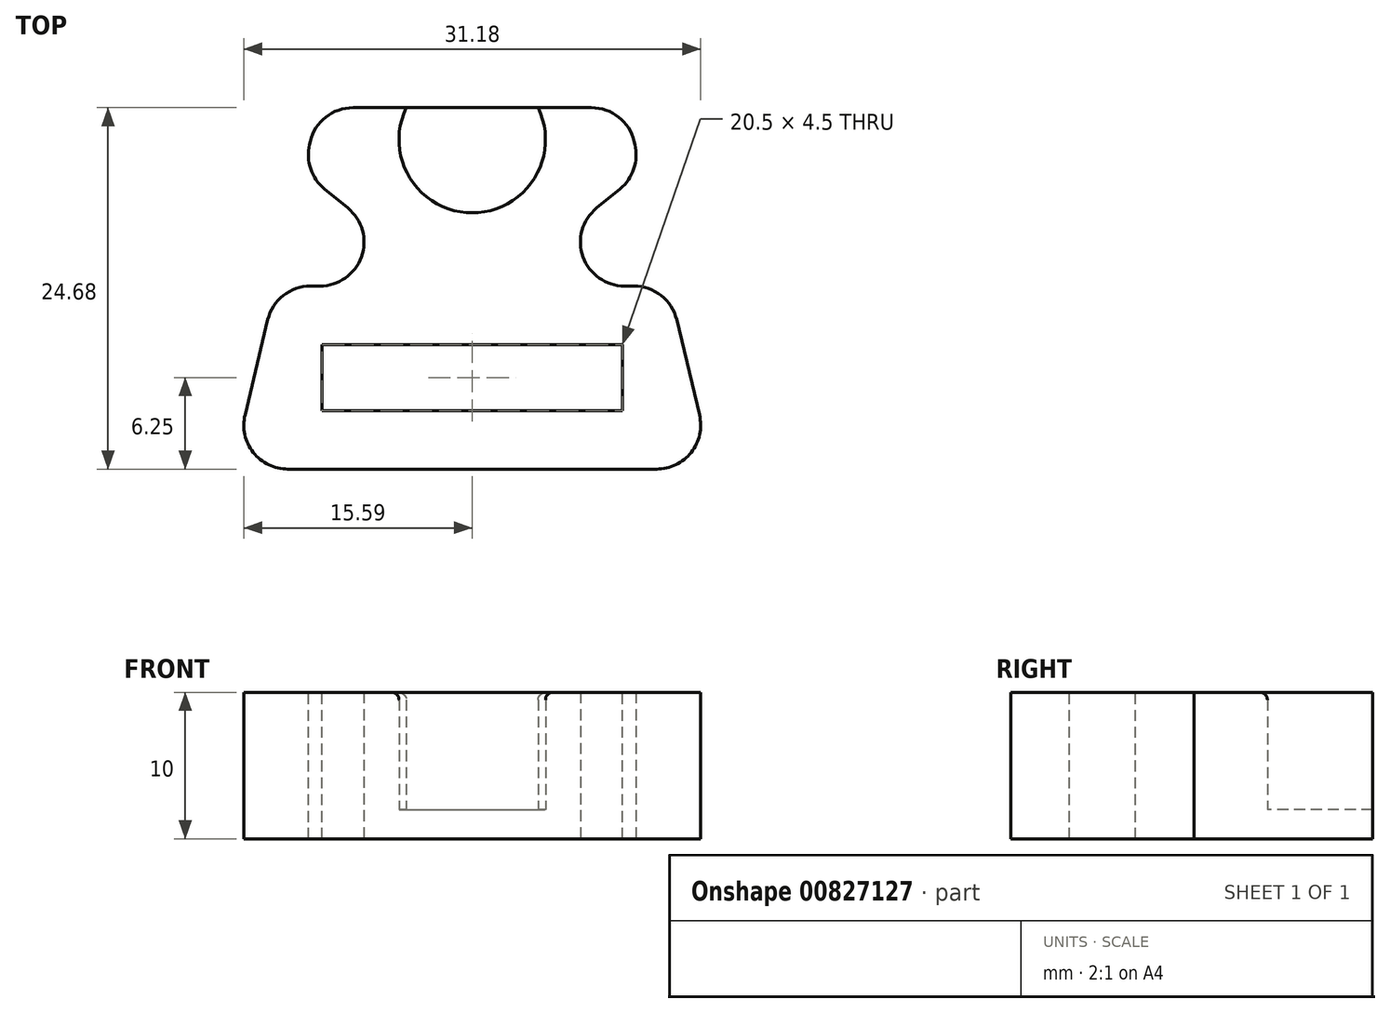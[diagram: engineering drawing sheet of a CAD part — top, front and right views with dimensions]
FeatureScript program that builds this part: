
annotation { "Feature Type Name" : "Feature", "Feature Type Description" : "" }
export const myFeature = defineFeature(function(context is Context, id is Id, definition is map)
    precondition{}
    {
        {
            var Q0;
            Q0=qCreatedBy(makeId("Top.planeOp"),FACE);
            var sketch = newSketch(context, id + "F0", { "sketchPlane" : qUnion([Q0])});
            skArc(sketch, "E0", {"start": v(-4.5, 2.18) * mm, "mid": v(0, -5) * mm, "end": v(4.5, 2.18) * mm});
            skLineSegment(sketch, "E1", {"start": v(4.5, 2.18) * mm, "end": v(10.5, 2.18) * mm});
            skLineSegment(sketch, "E2", {"start": v(-4.5, 2.18) * mm, "end": v(-10.5, 2.18) * mm});
            skLineSegment(sketch, "E3", {"start": v(-10.5, 2.18) * mm, "end": v(-16.4, -22.5) * mm});
            skLineSegment(sketch, "E4", {"start": v(-16.4, -22.5) * mm, "end": v(16.4, -22.5) * mm});
            skLineSegment(sketch, "E5", {"start": v(16.4, -22.5) * mm, "end": v(10.5, 2.18) * mm});
            skLineSegment(sketch, "E6.bottom", {"start": v(10.25, -18.5) * mm, "end": v(-10.25, -18.5) * mm});
            skLineSegment(sketch, "E6.top", {"start": v(10.25, -14) * mm, "end": v(-10.25, -14) * mm});
            skLineSegment(sketch, "E6.left", {"start": v(10.25, -18.5) * mm, "end": v(10.25, -14) * mm});
            skLineSegment(sketch, "E6.right", {"start": v(-10.25, -18.5) * mm, "end": v(-10.25, -14) * mm});
            skPoint(sketch, "E6.middle", {"position": v(0, -16.25) * mm});
            skLineSegment(sketch, "E7", {"start": v(0, 0) * mm, "end": v(5, 0) * mm, "construction": true});
            skLineSegment(sketch, "E8", {"start": v(-4.5, 2.18) * mm, "end": v(4.5, 2.18) * mm});
            skLineSegment(sketch, "E9", {"start": v(11.54, -2.17) * mm, "end": v(2, -10) * mm});
            skLineSegment(sketch, "E10", {"start": v(2, -10) * mm, "end": v(13.4, -10) * mm});
            skLineSegment(sketch, "E11", {"start": v(-11.54, -2.17) * mm, "end": v(-2, -10) * mm});
            skLineSegment(sketch, "E12", {"start": v(-2, -10) * mm, "end": v(-13.4, -10) * mm});
            skLineSegment(sketch, "E13", {"start": v(0, -16.25) * mm, "end": v(2, -10) * mm, "construction": true});
            skLineSegment(sketch, "E14", {"start": v(-2, -10) * mm, "end": v(0, -16.25) * mm, "construction": true});
            skSolve(sketch);
        }
        {
            var Q0;
            Q0=makeQuery(id+"F0.imprint","IMPRINT",FACE,{"disambiguationData":[TD([[makeQuery(id+"F0.imprint","IMPRINT",EDGE,{"derivedFrom":sQuery(id+"F0.wireOp",EDGE,"E0")}),-1.0]])]});
            var Q1;
            Q1=makeQuery(id+"F0.imprint","IMPRINT",FACE,{"disambiguationData":[TD([[makeQuery(id+"F0.imprint","IMPRINT",EDGE,{"derivedFrom":sQuery(id+"F0.wireOp",EDGE,"E0")}),1.0]])]});
            extrude(context, id + "F1", {"entities" : qUnion([Q0, Q1]), "oppositeDirection" : true, "depth" : 5 * mm, "offsetDistance" : 25 * mm});
        }
        {
            var Q0;
            Q0=makeQuery(id+"F0.imprint","IMPRINT",FACE,{"disambiguationData":[TD([[makeQuery(id+"F0.imprint","IMPRINT",EDGE,{"derivedFrom":sQuery(id+"F0.wireOp",EDGE,"E0")}),-1.0]])]});
            extrude(context, id + "F2", {"entities" : qUnion([Q0]), "operationType" : NewBodyOperationType.ADD, "depth" : 5 * mm, "offsetDistance" : 25 * mm});
        }
        {
            var Q0;
            {var subQ0=sQuery(id+"F0.wireOp",EDGE,"E4");var subQ1=sQuery(id+"F0.wireOp",EDGE,"E3");Q0=makeQuery(id+"F2.boolean.opBoolean","MERGE",EDGE,{"derivedFrom":[makeQuery(id+"F1.opExtrude","SWEPT_EDGE",EDGE,{"disambiguationData":[OSD([subQ1,subQ0])]}),makeQuery(id+"F2.opExtrude","SWEPT_EDGE",EDGE,{"disambiguationData":[OSD([subQ1,subQ0])]})]});}
            var Q1;
            {var subQ0=sQuery(id+"F0.wireOp",EDGE,"E5");var subQ1=sQuery(id+"F0.wireOp",EDGE,"E4");Q1=makeQuery(id+"F2.boolean.opBoolean","MERGE",EDGE,{"derivedFrom":[makeQuery(id+"F1.opExtrude","SWEPT_EDGE",EDGE,{"disambiguationData":[OSD([subQ1,subQ0])]}),makeQuery(id+"F2.opExtrude","SWEPT_EDGE",EDGE,{"disambiguationData":[OSD([subQ1,subQ0])]})]});}
            var Q2;
            {var subQ0=sQuery(id+"F0.wireOp",EDGE,"E3");var subQ1=sQuery(id+"F0.wireOp",EDGE,"E2");Q2=makeQuery(id+"F2.boolean.opBoolean","MERGE",EDGE,{"derivedFrom":[makeQuery(id+"F1.opExtrude","SWEPT_EDGE",EDGE,{"disambiguationData":[OSD([subQ1,subQ0])]}),makeQuery(id+"F2.opExtrude","SWEPT_EDGE",EDGE,{"disambiguationData":[OSD([subQ1,subQ0])]})]});}
            var Q3;
            {var subQ0=sQuery(id+"F0.wireOp",EDGE,"E5");var subQ1=sQuery(id+"F0.wireOp",EDGE,"E1");Q3=makeQuery(id+"F2.boolean.opBoolean","MERGE",EDGE,{"derivedFrom":[makeQuery(id+"F1.opExtrude","SWEPT_EDGE",EDGE,{"disambiguationData":[OSD([subQ1,subQ0])]}),makeQuery(id+"F2.opExtrude","SWEPT_EDGE",EDGE,{"disambiguationData":[OSD([subQ1,subQ0])]})]});}
            var Q4;
            {var subQ0=sQuery(id+"F0.wireOp",EDGE,"E12");var subQ1=sQuery(id+"F0.wireOp",EDGE,"E11");Q4=makeQuery(id+"F2.boolean.opBoolean","MERGE",EDGE,{"derivedFrom":[makeQuery(id+"F1.opExtrude","SWEPT_EDGE",EDGE,{"disambiguationData":[OSD([subQ1,subQ0])]}),makeQuery(id+"F2.opExtrude","SWEPT_EDGE",EDGE,{"disambiguationData":[OSD([subQ1,subQ0])]})]});}
            var Q5;
            {var subQ0=sQuery(id+"F0.wireOp",EDGE,"E12");var subQ1=sQuery(id+"F0.wireOp",EDGE,"E3");Q5=makeQuery(id+"F2.boolean.opBoolean","MERGE",EDGE,{"derivedFrom":[makeQuery(id+"F1.opExtrude","SWEPT_EDGE",EDGE,{"disambiguationData":[OSD([subQ1,subQ0])]}),makeQuery(id+"F2.opExtrude","SWEPT_EDGE",EDGE,{"disambiguationData":[OSD([subQ1,subQ0])]})]});}
            var Q6;
            {var subQ0=sQuery(id+"F0.wireOp",EDGE,"E11");var subQ1=sQuery(id+"F0.wireOp",EDGE,"E3");Q6=makeQuery(id+"F2.boolean.opBoolean","MERGE",EDGE,{"derivedFrom":[makeQuery(id+"F1.opExtrude","SWEPT_EDGE",EDGE,{"disambiguationData":[OSD([subQ1,subQ0])]}),makeQuery(id+"F2.opExtrude","SWEPT_EDGE",EDGE,{"disambiguationData":[OSD([subQ1,subQ0])]})]});}
            var Q7;
            {var subQ0=sQuery(id+"F0.wireOp",EDGE,"E9");var subQ1=sQuery(id+"F0.wireOp",EDGE,"E5");Q7=makeQuery(id+"F2.boolean.opBoolean","MERGE",EDGE,{"derivedFrom":[makeQuery(id+"F1.opExtrude","SWEPT_EDGE",EDGE,{"disambiguationData":[OSD([subQ1,subQ0])]}),makeQuery(id+"F2.opExtrude","SWEPT_EDGE",EDGE,{"disambiguationData":[OSD([subQ1,subQ0])]})]});}
            var Q8;
            {var subQ0=sQuery(id+"F0.wireOp",EDGE,"E10");var subQ1=sQuery(id+"F0.wireOp",EDGE,"E5");Q8=makeQuery(id+"F2.boolean.opBoolean","MERGE",EDGE,{"derivedFrom":[makeQuery(id+"F1.opExtrude","SWEPT_EDGE",EDGE,{"disambiguationData":[OSD([subQ1,subQ0])]}),makeQuery(id+"F2.opExtrude","SWEPT_EDGE",EDGE,{"disambiguationData":[OSD([subQ1,subQ0])]})]});}
            var Q9;
            {var subQ0=sQuery(id+"F0.wireOp",EDGE,"E10");var subQ1=sQuery(id+"F0.wireOp",EDGE,"E9");Q9=makeQuery(id+"F2.boolean.opBoolean","MERGE",EDGE,{"derivedFrom":[makeQuery(id+"F1.opExtrude","SWEPT_EDGE",EDGE,{"disambiguationData":[OSD([subQ1,subQ0])]}),makeQuery(id+"F2.opExtrude","SWEPT_EDGE",EDGE,{"disambiguationData":[OSD([subQ1,subQ0])]})]});}
            fillet(context, id + "F3", {"entities" : qUnion([Q0, Q1, Q2, Q3, Q4, Q5, Q6, Q7, Q8, Q9]), "tangentPropagation" : true, "radius" : 3 * mm, "defaultsChanged" : true, "vertexSettings" : [], "allowEdgeOverflow" : false});
        }
        {
            var Q0;
            Q0=makeQuery(id+"F2.opExtrude","CAP_EDGE",EDGE,{"disambiguationData":[OSD([sQuery(id+"F0.wireOp",EDGE,"E0")])],"isStart":false});
            fillet(context, id + "F4", {"entities" : qUnion([Q0]), "tangentPropagation" : true, "radius" : 0.5 * mm, "defaultsChanged" : true, "vertexSettings" : [], "allowEdgeOverflow" : false});
        }
        {
            var Q0;
            Q0=makeQuery(id+"F1.opExtrude","CAP_FACE",FACE,{"disambiguationData":[OSD([sQuery(id+"F0.wireOp",EDGE,"E1"),sQuery(id+"F0.wireOp",EDGE,"E2"),sQuery(id+"F0.wireOp",EDGE,"E3"),sQuery(id+"F0.wireOp",EDGE,"E4"),sQuery(id+"F0.wireOp",EDGE,"E5"),sQuery(id+"F0.wireOp",EDGE,"E6.bottom"),sQuery(id+"F0.wireOp",EDGE,"E6.top"),sQuery(id+"F0.wireOp",EDGE,"E6.left"),sQuery(id+"F0.wireOp",EDGE,"E6.right"),sQuery(id+"F0.wireOp",EDGE,"E8")])],"isStart":true});
            extrude(context, id + "F5", {"entities" : qUnion([Q0]), "operationType" : NewBodyOperationType.REMOVE, "oppositeDirection" : true, "depth" : 3 * mm, "offsetDistance" : 25 * mm});
        }
    });
